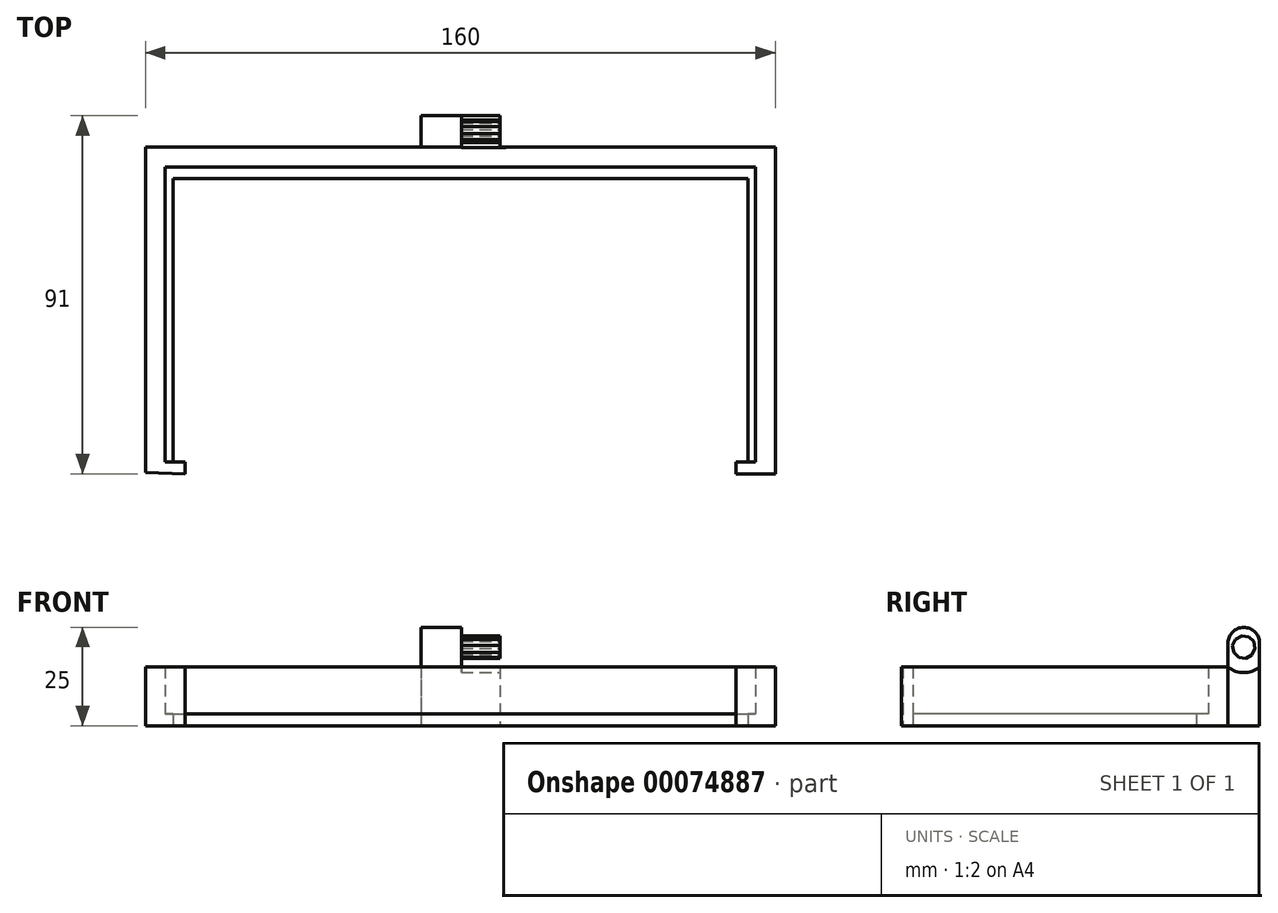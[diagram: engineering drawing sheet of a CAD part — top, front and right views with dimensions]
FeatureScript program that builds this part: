
annotation { "Feature Type Name" : "Feature", "Feature Type Description" : "" }
export const myFeature = defineFeature(function(context is Context, id is Id, definition is map)
    precondition{}
    {
        {
            var Q0;
            Q0=qCreatedBy(makeId("Top.planeOp"),FACE);
            var sketch = newSketch(context, id + "F0", { "sketchPlane" : qUnion([Q0])});
            skLineSegment(sketch, "E0", {"start": v(-91.6, 32.14) * mm, "end": v(-91.6, -50.45) * mm});
            skLineSegment(sketch, "E1", {"start": v(-91.6, -50.45) * mm, "end": v(-81.6, -50.86) * mm});
            skLineSegment(sketch, "E2", {"start": v(-81.6, -50.86) * mm, "end": v(-81.6, -47.86) * mm});
            skLineSegment(sketch, "E3", {"start": v(-81.6, -47.86) * mm, "end": v(-86.6, -47.86) * mm});
            skLineSegment(sketch, "E4", {"start": v(-86.6, -47.86) * mm, "end": v(-86.6, 27.14) * mm});
            skLineSegment(sketch, "E5", {"start": v(-86.6, 27.14) * mm, "end": v(63.4, 27.14) * mm});
            skLineSegment(sketch, "E6", {"start": v(63.4, 27.14) * mm, "end": v(63.4, -47.86) * mm});
            skLineSegment(sketch, "E7", {"start": v(63.4, -47.86) * mm, "end": v(58.4, -47.86) * mm});
            skLineSegment(sketch, "E8", {"start": v(58.4, -47.86) * mm, "end": v(58.4, -50.86) * mm});
            skLineSegment(sketch, "E9", {"start": v(58.4, -50.86) * mm, "end": v(68.4, -50.86) * mm});
            skLineSegment(sketch, "E10", {"start": v(68.4, -50.86) * mm, "end": v(68.4, 32.14) * mm});
            skLineSegment(sketch, "E11", {"start": v(68.4, 32.14) * mm, "end": v(-91.6, 32.14) * mm});
            skLineSegment(sketch, "E12", {"start": v(-84.6, 27.14) * mm, "end": v(-84.6, -47.86) * mm});
            skLineSegment(sketch, "E13", {"start": v(61.4, 27.14) * mm, "end": v(61.4, -47.86) * mm});
            skLineSegment(sketch, "E14", {"start": v(-84.6, 24.14) * mm, "end": v(61.4, 24.14) * mm});
            skLineSegment(sketch, "E15", {"start": v(-21.6, 32.14) * mm, "end": v(-21.6, 40.14) * mm});
            skLineSegment(sketch, "E16", {"start": v(-21.6, 40.14) * mm, "end": v(-1.6, 40.14) * mm});
            skLineSegment(sketch, "E17", {"start": v(-1.6, 40.14) * mm, "end": v(-1.6, 32.14) * mm});
            skSolve(sketch);
        }
        {
            var Q0;
            Q0=makeQuery(id+"F0.imprint","IMPRINT",FACE,{"disambiguationData":[TD([[makeQuery(id+"F0.imprint","IMPRINT",EDGE,{"derivedFrom":sQuery(id+"F0.wireOp",EDGE,"E0")}),1.0]])]});
            extrude(context, id + "F1", {"entities" : qUnion([Q0]), "depth" : 15 * mm});
        }
        {
            var Q0;
            {var subQ0=sQuery(id+"F0.wireOp",EDGE,"E4");Q0=makeQuery(id+"F0.imprint","IMPRINT",FACE,{"disambiguationData":[TD([[makeQuery(id+"F0.imprint","IMPRINT",EDGE,{"derivedFrom":subQ0}),-1.0]])]});}
            var Q1;
            {var subQ0=sQuery(id+"F0.wireOp",EDGE,"E6");Q1=makeQuery(id+"F0.imprint","IMPRINT",FACE,{"disambiguationData":[TD([[makeQuery(id+"F0.imprint","IMPRINT",EDGE,{"derivedFrom":subQ0}),-1.0]])]});}
            extrude(context, id + "F2", {"entities" : qUnion([Q0, Q1]), "operationType" : NewBodyOperationType.ADD, "depth" : 3 * mm});
        }
        {
            var Q0;
            {var subQ5=sQuery(id+"F0.wireOp",EDGE,"E14");Q0=makeQuery(id+"F0.imprint","IMPRINT",FACE,{"disambiguationData":[TD([[makeQuery(id+"F0.imprint","IMPRINT",EDGE,{"derivedFrom":subQ5}),1.0]])]});}
            extrude(context, id + "F3", {"entities" : qUnion([Q0]), "operationType" : NewBodyOperationType.ADD, "depth" : 3 * mm});
        }
        {
            var Q0;
            {var subQ0=sQuery(id+"F0.wireOp",EDGE,"E15");Q0=makeQuery(id+"F0.imprint","IMPRINT",FACE,{"disambiguationData":[TD([[makeQuery(id+"F0.imprint","IMPRINT",EDGE,{"derivedFrom":subQ0}),-1.0]])]});}
            extrude(context, id + "F4", {"entities" : qUnion([Q0]), "operationType" : NewBodyOperationType.ADD, "depth" : 25 * mm});
        }
        {
            var Q0;
            Q0=qCreatedBy(makeId("Right.planeOp"),FACE);
            var sketch = newSketch(context, id + "F5", { "sketchPlane" : qUnion([Q0])});
            skCircle(sketch, "E18", {"center": v(36.14, 20) * mm, "radius": 6.5 * mm});
            skCircle(sketch, "E19.cCircle", {"center": v(36.14, 20) * mm, "radius": 2.75 * mm, "construction": true});
            skLineSegment(sketch, "E19.0", {"start": v(34.03, 21.98) * mm, "end": v(35.6, 22.84) * mm});
            skLineSegment(sketch, "E19.1", {"start": v(35.6, 22.84) * mm, "end": v(37.37, 22.62) * mm});
            skLineSegment(sketch, "E19.2", {"start": v(37.37, 22.62) * mm, "end": v(38.67, 21.4) * mm});
            skLineSegment(sketch, "E19.3", {"start": v(38.67, 21.4) * mm, "end": v(39, 19.64) * mm});
            skLineSegment(sketch, "E19.4", {"start": v(39, 19.64) * mm, "end": v(38.25, 18.02) * mm});
            skLineSegment(sketch, "E19.5", {"start": v(38.25, 18.02) * mm, "end": v(36.68, 17.16) * mm});
            skLineSegment(sketch, "E19.6", {"start": v(36.68, 17.16) * mm, "end": v(34.9, 17.38) * mm});
            skLineSegment(sketch, "E19.7", {"start": v(34.9, 17.38) * mm, "end": v(33.6, 18.6) * mm});
            skLineSegment(sketch, "E19.8", {"start": v(33.6, 18.6) * mm, "end": v(33.27, 20.36) * mm});
            skLineSegment(sketch, "E19.9", {"start": v(33.27, 20.36) * mm, "end": v(34.03, 21.98) * mm});
            skPoint(sketch, "E19.0.midPoint", {"position": v(34.82, 22.41) * mm});
            skSolve(sketch);
        }
        {
            var Q0;
            Q0=makeQuery(id+"F5.imprint","IMPRINT",FACE,{"disambiguationData":[TD([[makeQuery(id+"F5.imprint","IMPRINT",EDGE,{"derivedFrom":sQuery(id+"F5.wireOp",EDGE,"E18")}),1.0]])]});
            extrude(context, id + "F6", {"entities" : qUnion([Q0]), "operationType" : NewBodyOperationType.REMOVE, "oppositeDirection" : true, "depth" : 11.37 * mm});
        }
        {
            var Q0;
            Q0=makeQuery(id+"F4.opExtrude","CAP_EDGE",EDGE,{"disambiguationData":[OSD([sQuery(id+"F0.wireOp",EDGE,"E16")])],"isStart":false});
            var Q1;
            Q1=makeQuery(id+"F4.opExtrude","CAP_EDGE",EDGE,{"disambiguationData":[OSD([sQuery(id+"F0.wireOp",EDGE,"E11")])],"isStart":false});
            fillet(context, id + "F7", {"entities" : qUnion([Q0, Q1]), "radius" : 4 * mm, "tangentPropagation" : true, "allowEdgeOverflow" : false});
        }
    });
